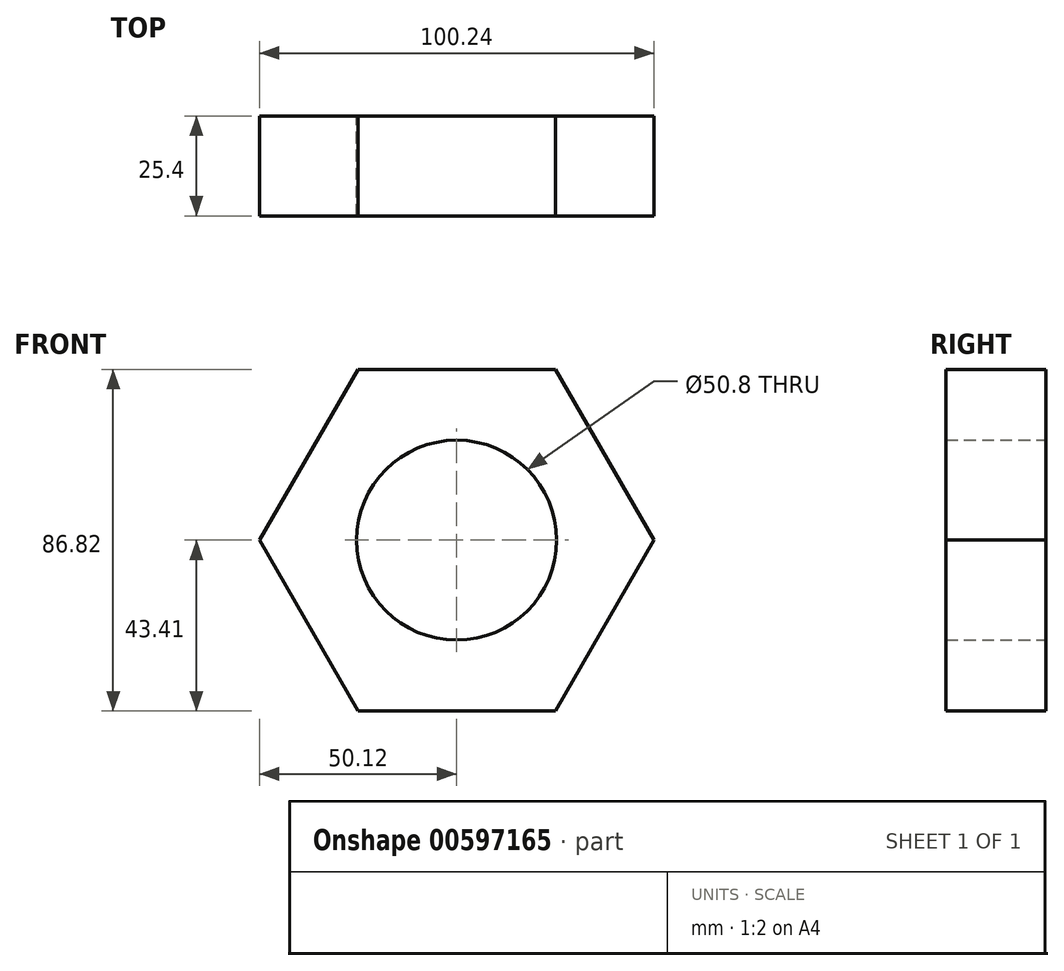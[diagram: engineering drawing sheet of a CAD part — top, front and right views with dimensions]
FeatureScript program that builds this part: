
annotation { "Feature Type Name" : "Feature", "Feature Type Description" : "" }
export const myFeature = defineFeature(function(context is Context, id is Id, definition is map)
    precondition{}
    {
        {
            var Q0;
            Q0=qCreatedBy(makeId("Front.planeOp"),FACE);
            var sketch = newSketch(context, id + "F0", { "sketchPlane" : qUnion([Q0])});
            skLineSegment(sketch, "E0.0", {"start": v(25.06, -43.4) * mm, "end": v(-25.06, -43.4) * mm});
            skLineSegment(sketch, "E0.1", {"start": v(-25.06, -43.4) * mm, "end": v(-50.12, 0) * mm});
            skLineSegment(sketch, "E0.2", {"start": v(-50.12, 0) * mm, "end": v(-25.06, 43.4) * mm});
            skLineSegment(sketch, "E0.3", {"start": v(-25.06, 43.4) * mm, "end": v(25.06, 43.4) * mm});
            skLineSegment(sketch, "E0.4", {"start": v(25.06, 43.4) * mm, "end": v(50.12, 0) * mm});
            skLineSegment(sketch, "E0.5", {"start": v(50.12, 0) * mm, "end": v(25.06, -43.4) * mm});
            skPoint(sketch, "E0.0.midPoint", {"position": v(0, -43.4) * mm});
            skCircle(sketch, "E1", {"center": v(0, 0) * mm, "radius": 25.4 * mm});
            skSolve(sketch);
        }
        {
            var Q0;
            Q0=makeQuery(id+"F0.imprint","IMPRINT",FACE,{"disambiguationData":[TD([[makeQuery(id+"F0.imprint","IMPRINT",EDGE,{"derivedFrom":sQuery(id+"F0.wireOp",EDGE,"E0.0")}),-1.0]])]});
            extrude(context, id + "F1", {"entities" : qUnion([Q0]), "depth" : 25.4 * mm, "offsetDistance" : 25.4 * mm});
        }
    });
